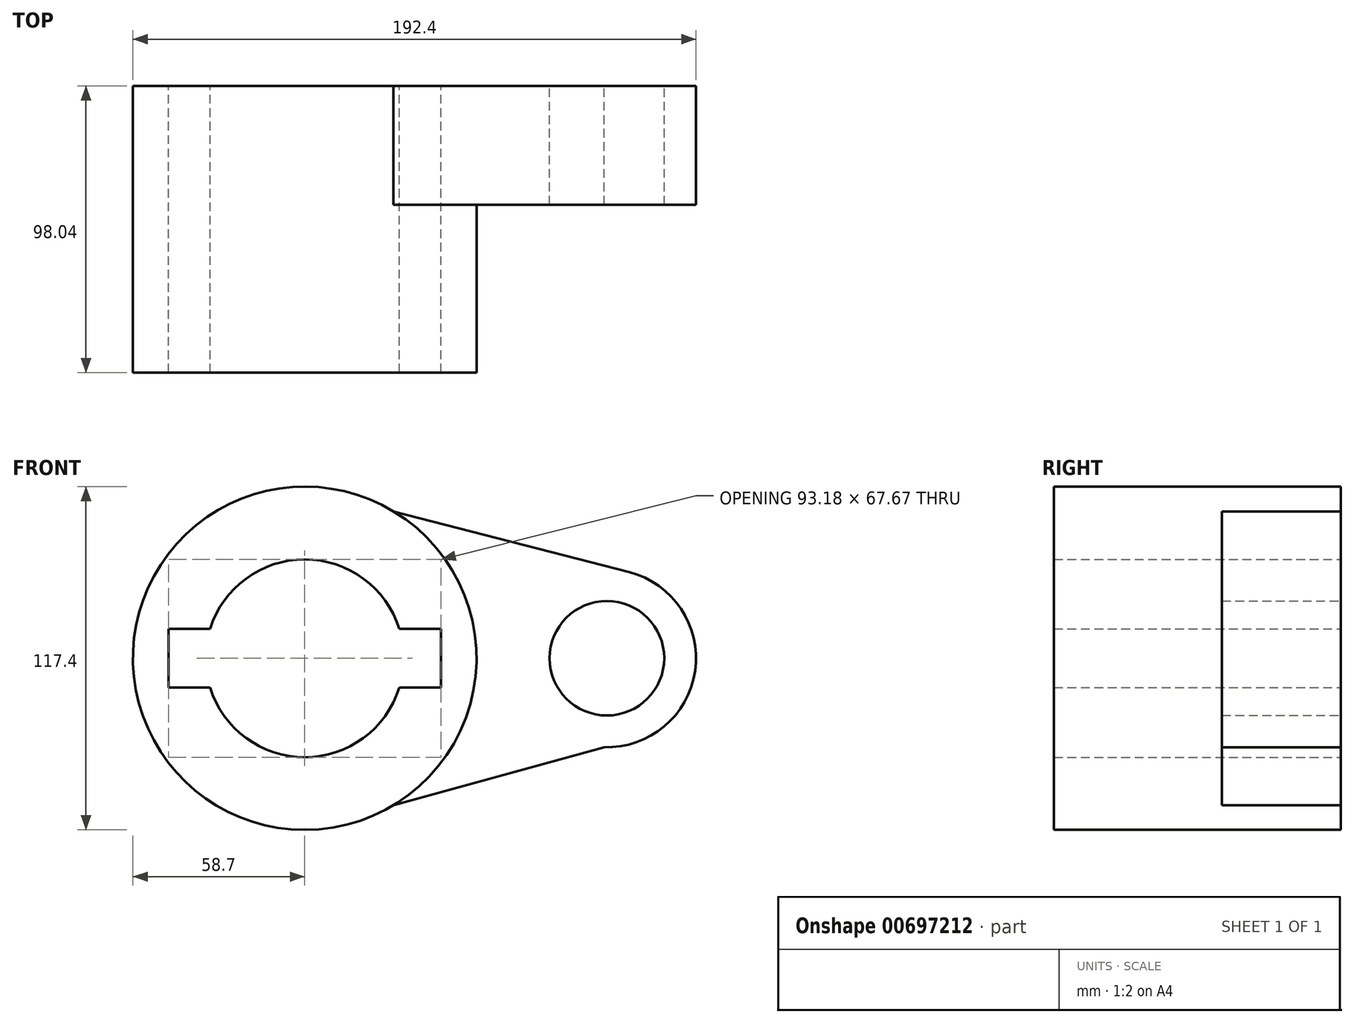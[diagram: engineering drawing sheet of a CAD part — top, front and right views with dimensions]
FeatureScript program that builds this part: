
annotation { "Feature Type Name" : "Feature", "Feature Type Description" : "" }
export const myFeature = defineFeature(function(context is Context, id is Id, definition is map)
    precondition{}
    {
        {
            var Q0;
            Q0=qCreatedBy(makeId("Front.planeOp"),FACE);
            var sketch = newSketch(context, id + "F0", { "sketchPlane" : qUnion([Q0])});
            skCircle(sketch, "E0", {"center": v(0, 0) * mm, "radius": 58.7 * mm});
            skCircle(sketch, "E1", {"center": v(103.25, 0) * mm, "radius": 30.45 * mm});
            skLineSegment(sketch, "E2", {"start": v(30.36, 50.25) * mm, "end": v(110.86, 29.48) * mm});
            skLineSegment(sketch, "E3", {"start": v(30.34, -50.25) * mm, "end": v(102.25, -30.43) * mm});
            skCircle(sketch, "E4", {"center": v(0, 0) * mm, "radius": 33.83 * mm});
            skCircle(sketch, "E5", {"center": v(103.25, 0) * mm, "radius": 19.58 * mm});
            skLineSegment(sketch, "E6.bottom", {"start": v(-46.6, -10.07) * mm, "end": v(46.6, -10.07) * mm});
            skLineSegment(sketch, "E6.top", {"start": v(-46.6, 10.07) * mm, "end": v(46.6, 10.07) * mm});
            skLineSegment(sketch, "E6.left", {"start": v(-46.6, -10.07) * mm, "end": v(-46.6, 10.07) * mm});
            skLineSegment(sketch, "E6.right", {"start": v(46.6, -10.07) * mm, "end": v(46.6, 10.07) * mm});
            skSolve(sketch);
        }
        {
            var Q0;
            Q0 = qSketchRegion(id + "F0", true);
            extrude(context, id + "F1", {"entities" : qUnion([Q0]), "depth" : 40.64 * mm, "offsetDistance" : 25.4 * mm});
        }
        {
            var Q0;
            {var subQ7=sQuery(id+"F0.wireOp",EDGE,"E6.left");Q0=makeQuery(id+"F0.imprint","IMPRINT",FACE,{"disambiguationData":[TD([[makeQuery(id+"F0.imprint","IMPRINT",EDGE,{"derivedFrom":subQ7}),1.0]])]});}
            extrude(context, id + "F2", {"entities" : qUnion([Q0]), "operationType" : NewBodyOperationType.ADD, "depth" : 98.04 * mm, "offsetDistance" : 25.4 * mm});
        }
    });
